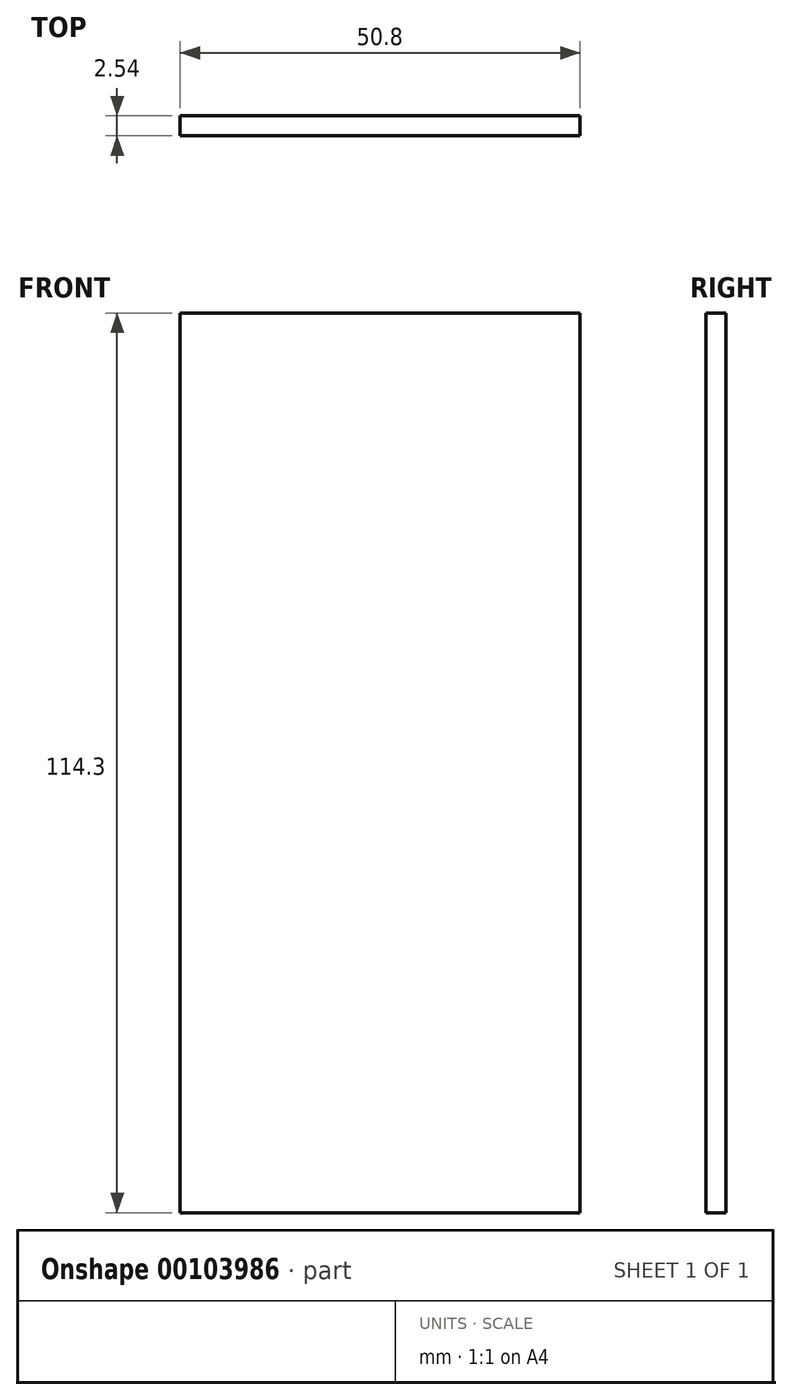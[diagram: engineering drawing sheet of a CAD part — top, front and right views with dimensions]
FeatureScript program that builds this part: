
annotation { "Feature Type Name" : "Feature", "Feature Type Description" : "" }
export const myFeature = defineFeature(function(context is Context, id is Id, definition is map)
    precondition{}
    {
        {
            var Q0;
            Q0=qCreatedBy(makeId("Front.planeOp"),FACE);
            var sketch = newSketch(context, id + "F0", { "sketchPlane" : qUnion([Q0])});
            skLineSegment(sketch, "E0.bottom", {"start": v(-39.45, 53.2) * mm, "end": v(11.35, 53.2) * mm});
            skLineSegment(sketch, "E0.top", {"start": v(-39.45, -61.1) * mm, "end": v(11.35, -61.1) * mm});
            skLineSegment(sketch, "E0.left", {"start": v(-39.45, 53.2) * mm, "end": v(-39.45, -61.1) * mm});
            skLineSegment(sketch, "E0.right", {"start": v(11.35, 53.2) * mm, "end": v(11.35, -61.1) * mm});
            skSolve(sketch);
        }
        {
            var Q0;
            Q0=makeQuery(id+"F0.imprint","IMPRINT",FACE,{"disambiguationData":[TD([[makeQuery(id+"F0.imprint","IMPRINT",EDGE,{"derivedFrom":sQuery(id+"F0.wireOp",EDGE,"E0.bottom")}),-1.0]])]});
            extrude(context, id + "F1", {"entities" : qUnion([Q0]), "depth" : 2.54 * mm});
        }
    });
